# Revit family: QF-Water_Processor-OptiPure-BWS100
name_source: partatom
category: Specialty Equipment
revit_build: Autodesk Revit 2017 (Build: 20160225_1515(x64)
units: mm (PartAtom-declared; Revit-internal decimal feet)

## family parameters
Always vertical = Yes
Cut with Voids When Loaded = No
OmniClass Number = 23.40.40.14
OmniClass Title = Food Service Equipment
Part Type = Normal
Room Calculation Point = No
Round Connector Dimension = Use Diameter
Shared = No
Work Plane-Based = No

## types (1)
- BWS100
    Assembly Code = E1090300
    Body Material = Mounting
    Clearance Material = Clearance
    Cold Water Maximum Pressure = 85.00 psi
    Cold Water Minimum Pressure = 50.00 psi
    Cold Water Size = 0"
    Description = WATER FILTRATION SYSTEM
    Feed Temperature Range = 40-100° F
    Filtered Water Flow = 0 GPM
    Filtered Water Supply Size = 0"
    Height = 20.22 "
    Indirect Waste Flow = 2 GPM
    Indirect Waste Size = 0"
    Keynote = 11400
    Length = 18.26 "
    Manufacturer = OPTIPURE
    Material = Plastic
    Model = 164-00100 - BWS100 SYS
    Type Comments = BLENDED WATER REVERSE OSMOSIS
    URL = WWW.OPTIPUREWATER.COM
    Weight in Pounds = 25
    Width = 5.93 "

## geometry (parser evidence)
native form markers: Sweep x3
no freeform markers — native parametric forms only
